# Revit family: Digidim 4-Channel Ballast Controller_474
name_source: partatom
category: Electrical Fixtures
revit_build: Autodesk Revit 2018 (Build: 20170223_1515(x64)
units: mm (PartAtom-declared; Revit-internal decimal feet)

## family parameters
Always vertical = Yes
Cut with Voids When Loaded = No
Maintain Annotation Orientation = No
OmniClass Number = 23.80.00.00
OmniClass Title = Electric Power and Lighting
Part Type = Normal
Room Calculation Point = No
Round Connector Dimension = Use Diameter
Shared = No
Work Plane-Based = Yes

## types (1)
- DIGIDIM 4-CHANNEL BALLAST CONTROLLER
    Ambient temperature = 0 °C to + 40 °C
    Communication = DALI, SDIM and DMX
    Connections: = Mains/relay/output: Solid core: up to 4 mm² Stranded: 2.5 mm²
DALI: 0.5 mm² – 1.5 mm²
Max. length: 300 m @ 1.5 mm²
SDIM/DMX: 0.22 mm² – 1.5 mm² low-loss
                  RS485 type (multistranded,
                  twisted and shielded).
                  Max. length: 1000 m (low-loss
                  cable). Examples: Belden 8102 or Alpha 6222C.
                  Note: One twisted pair for A
                  and B (85 Ω to 100 Ω impedance),
                  one core or twisted pair for 0 V,
                  and shield for screen.
    DALI consumption = 2 mA
    DALI: = According to DALI standard
IEC 62386, with Helvar additions
    DMX = DMX512-A protocol (max. refresh
rate: 33 Hz)
    Default Elevation = 0 mm  [stored 0 ft]
    Dimensions: = 160 mm × 90 mm × 58 mm
    EMC emission = EN 55015
    EMC immunity = EN 61547
    Environment = Complies with WEEE and RoHS directives.
    External protection = The mains supply must be
protected at 6 A maximum. The
relays must be protected by a
16 A Type C MCB maximum.
    Housing = DIN-rail case; 9U
    IP code: = IP30 (IP00 at terminals)
    Isolation = All connectors are isolated from
each other, except for SDIM/
DMX to Override, and ballast
output 1–2 to ballast output 3–4
    Mains Supply = 100 VAC – 240 VAC (nominal)
85 VAC – 264 VAC (absolute)
45 Hz – 65 Hz
    Manufacturer = Helvar
    Material = Polycarbonate/ABS mix, UL94 V–0
    Model = 474
    Mounting = DIN rail (installation in
switchgear/controlgear cabinet)
    Output = 0–10 V: Source 10 mA
1–10 V: Sink 100 mA
DALI/DSI®: (50 ballasts) Source 100 mA
PWM +/–: (50 ballasts) Source 100 mA
    Override = Wired override input
    Power consumption = 2.4 W (minimum) to 11 W
(all outputs fully loaded)
    Relative humidity = Max. 90 %, noncondensing
    Relay = Channels           :4
Relay contacts: High inrush (800 A at 200 µs),
                         single pole normally open
                        (SPNO)
Max. load per contact: 16 A resistive/incandescent;
                                      10 A HID (cos y = 0.6).
                                       For ballasts, quantity is
                                       limited by MCB: refer to the
                                       manufacturer’s data.
    SDIM: = According to Helvar SDIM
protocol
    Safety = EN 61347-2-11
    Storage temperature = −10 °C to + 70 °C
    Weight: = 280 g

note: [stored X ft] marks values corroborated as IEEE doubles in the binary element streams (Revit-internal decimal feet)

## geometry (parser evidence)
native form markers: Sweep x2
no freeform markers — native parametric forms only
